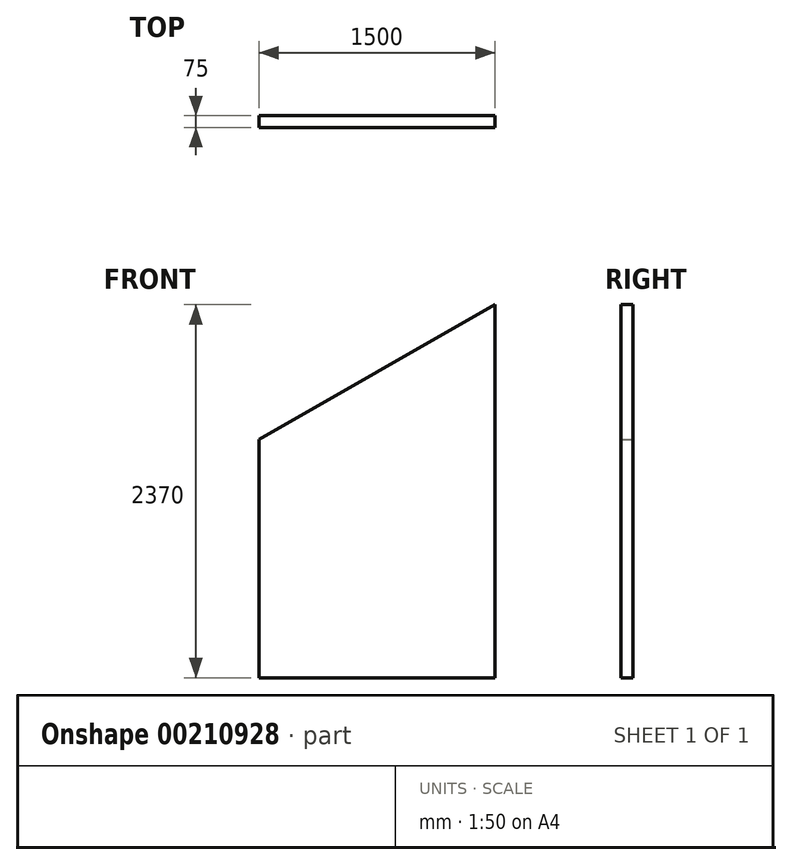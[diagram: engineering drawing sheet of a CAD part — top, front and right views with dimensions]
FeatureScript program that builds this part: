
annotation { "Feature Type Name" : "Feature", "Feature Type Description" : "" }
export const myFeature = defineFeature(function(context is Context, id is Id, definition is map)
    precondition{}
    {
        {
            var Q0;
            Q0=qCreatedBy(makeId("Front.planeOp"),FACE);
            var sketch = newSketch(context, id + "F0", { "sketchPlane" : qUnion([Q0])});
            skLineSegment(sketch, "E0.bottom", {"start": v(0, 0) * mm, "end": v(1500, 0) * mm});
            skLineSegment(sketch, "E0.right", {"start": v(1500, 0) * mm, "end": v(1500, 2370) * mm});
            skLineSegment(sketch, "E1", {"start": v(0, 1514) * mm, "end": v(1500, 2370) * mm});
            skLineSegment(sketch, "E2", {"start": v(0, 0) * mm, "end": v(0, 1514) * mm});
            skSolve(sketch);
        }
        {
            var Q0;
            Q0=makeQuery(id+"F0.imprint","IMPRINT",FACE,{"disambiguationData":[TD([[makeQuery(id+"F0.imprint","IMPRINT",EDGE,{"derivedFrom":sQuery(id+"F0.wireOp",EDGE,"E0.bottom")}),1.0]])]});
            extrude(context, id + "F1", {"entities" : qUnion([Q0]), "depth" : 75 * mm});
        }
    });
